# Revit family: Shower-Valve_Trim-KOHLER-PURIST-K-77926A_1
name_source: partatom
category: Plumbing Fixtures
revit_build: Autodesk Revit 2017 (Build: 20160225_1515(x64)
units: mm (PartAtom-declared; Revit-internal decimal feet)

## family parameters
Cut with Voids When Loaded = No
Host = Face
OmniClass Number = 23.27.31.00
OmniClass Title = Valves
Part Type = Normal
Room Calculation Point = No
Round Connector Dimension = Use Diameter
Shared = No

## types (5) — shared parameters
ADA Compliant = No
Assembly Code = D2020
CW Connection = Yes
Cold Water Inlet = Cold Water Inlet
Date Modified = 08/04/2021
Default Elevation = 36"
Description = BATH AND SHOWER MIXER W DIVERTER
Flow Rate = 0 GPM
HW Connection = Yes
Handle Clearance = 2 5/8"
Height = 7"
Hot Water Inlet = Hot Water Inlet
Length = 4 5/16"
Manufacturer = KOHLER Co.
Master Format 2014 = 23 09 13.33
Master Format 2014 Name = Control Valves
Material = Premium Metal Construction
Pressure = 0.00 psi
Product Name = AVID
Tempered Water Outlet 1 = Tempered Water Outlet 1
Tempered Water Outlet 2 = Tempered Water Outlet 2
URL = https://www.kohlerasiapacific.com
Vent Connection = No
Waste Connection = No
Waste Water Outlet = Waste Water Outlet
WaterSense Certified = No
Width = 7"

## per-type parameters (varying)
| type | Finish | Model | Type |
| CP-Polished Chrome | Kohler-Metal-CP-Polished_Chrome | K-77926A-CP | 1 |
| BN-Vibrant Brushed Nickel | Kohler-Metal-BN-Vibrant_Brushed_Nickel | K-77926A-BN | 2 |
| BV-Brushed Bronze | Kohler-Metal-BV-Brushed_Bronze | K-77926A-BV | 3 |
| PGD-Modern Polished Gold | Kohler-Metal-PGD-Modern_Polished_Gold | K-77926A-PGD | 4 |
| RGD-Polished Rose Gold | Kohler-Metal-RGD-Polished_Rose_Gold | K-77926A-RGD | 5 |

## geometry (parser evidence)
native form markers: Sweep x5
no freeform markers — native parametric forms only
